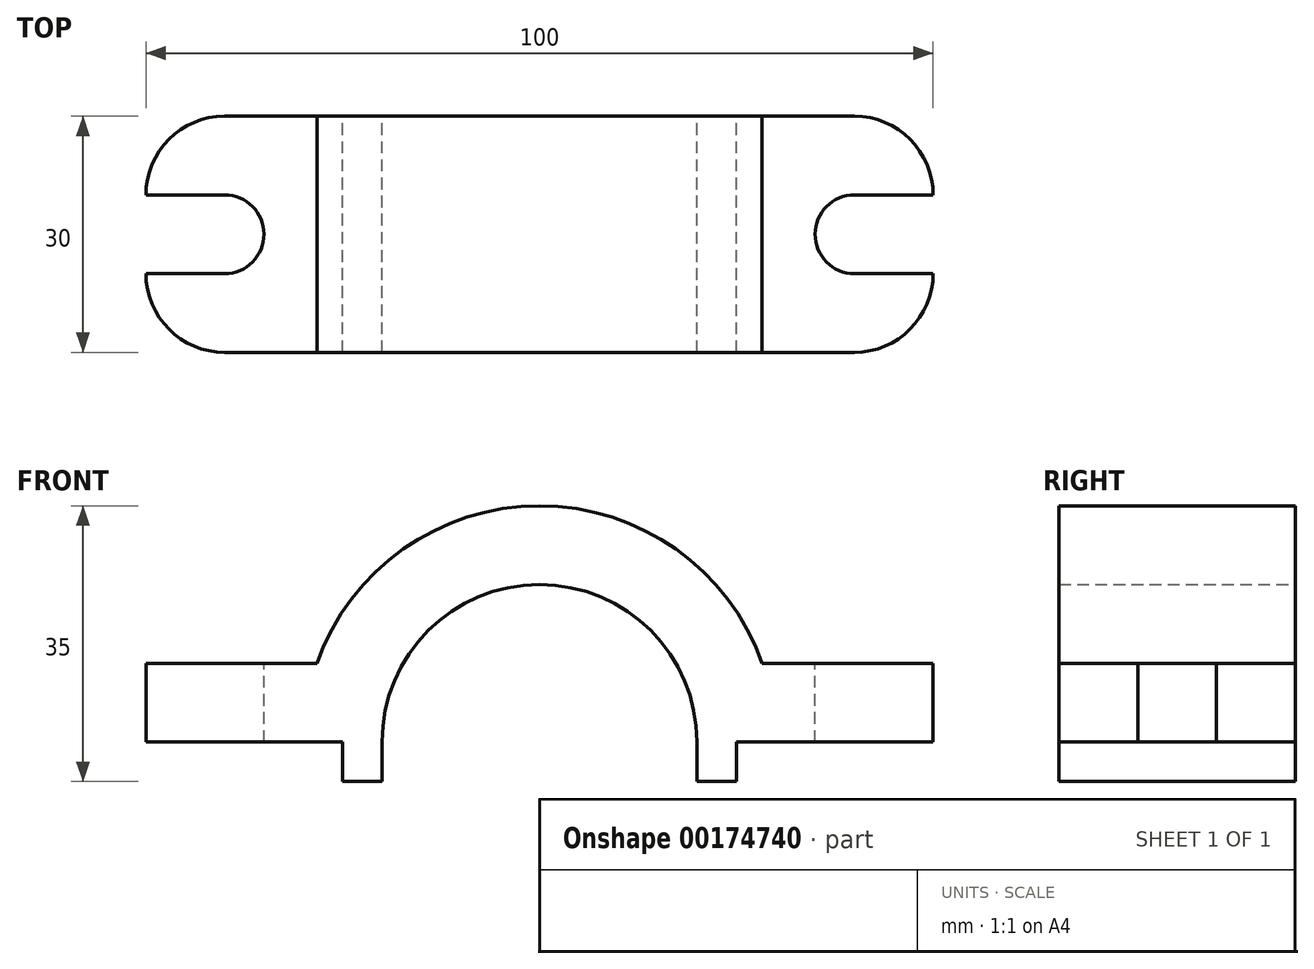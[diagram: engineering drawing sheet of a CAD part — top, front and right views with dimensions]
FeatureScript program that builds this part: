
annotation { "Feature Type Name" : "Feature", "Feature Type Description" : "" }
export const myFeature = defineFeature(function(context is Context, id is Id, definition is map)
    precondition{}
    {
        {
            var Q0;
            Q0=qCreatedBy(makeId("Front.planeOp"),FACE);
            var sketch = newSketch(context, id + "F0", { "sketchPlane" : qUnion([Q0])});
            skLineSegment(sketch, "E0.bottom", {"start": v(-50, 0) * mm, "end": v(-25, 0) * mm});
            skLineSegment(sketch, "E0.top", {"start": v(-50, 10) * mm, "end": v(-28.28, 10) * mm});
            skLineSegment(sketch, "E0.left", {"start": v(-50, 0) * mm, "end": v(-50, 10) * mm});
            skLineSegment(sketch, "E0.right", {"start": v(50, 0) * mm, "end": v(50, 10) * mm});
            skArc(sketch, "E1", {"start": v(28.28, 10) * mm, "mid": v(0, 30) * mm, "end": v(-28.28, 10) * mm});
            skLineSegment(sketch, "E2.trimOffspring", {"start": v(28.28, 10) * mm, "end": v(50, 10) * mm});
            skArc(sketch, "E3", {"start": v(20, 0) * mm, "mid": v(0, 20) * mm, "end": v(-20, 0) * mm});
            skLineSegment(sketch, "E4.trimOffspring", {"start": v(25, 0) * mm, "end": v(50, 0) * mm});
            skLineSegment(sketch, "E5.top", {"start": v(-20, -5) * mm, "end": v(-25, -5) * mm});
            skLineSegment(sketch, "E5.left", {"start": v(-20, 0) * mm, "end": v(-20, -5) * mm});
            skLineSegment(sketch, "E5.right", {"start": v(-25, 0) * mm, "end": v(-25, -5) * mm});
            skLineSegment(sketch, "E6.top", {"start": v(20, -5) * mm, "end": v(25, -5) * mm});
            skLineSegment(sketch, "E6.left", {"start": v(20, 0) * mm, "end": v(20, -5) * mm});
            skLineSegment(sketch, "E6.right", {"start": v(25, 0) * mm, "end": v(25, -5) * mm});
            skSolve(sketch);
        }
        {
            var Q0;
            Q0=makeQuery(id+"F0.imprint","IMPRINT",FACE,{"disambiguationData":[TD([[makeQuery(id+"F0.imprint","IMPRINT",EDGE,{"derivedFrom":sQuery(id+"F0.wireOp",EDGE,"E0.bottom")}),1.0]])]});
            extrude(context, id + "F1", {"entities" : qUnion([Q0]), "endBound" : BoundingType.SYMMETRIC, "depth" : 30 * mm});
        }
        {
            var Q0;
            Q0=makeQuery(id+"F1.opExtrude","CAP_EDGE",EDGE,{"disambiguationData":[OSD([sQuery(id+"F0.wireOp",EDGE,"E0.left")])],"isStart":false});
            var Q1;
            Q1=makeQuery(id+"F1.opExtrude","CAP_EDGE",EDGE,{"disambiguationData":[OSD([sQuery(id+"F0.wireOp",EDGE,"E0.right")])],"isStart":false});
            var Q2;
            Q2=makeQuery(id+"F1.opExtrude","CAP_EDGE",EDGE,{"disambiguationData":[OSD([sQuery(id+"F0.wireOp",EDGE,"E0.right")])],"isStart":true});
            var Q3;
            Q3=makeQuery(id+"F1.opExtrude","CAP_EDGE",EDGE,{"disambiguationData":[OSD([sQuery(id+"F0.wireOp",EDGE,"E0.left")])],"isStart":true});
            fillet(context, id + "F2", {"entities" : qUnion([Q0, Q1, Q2, Q3]), "radius" : 10 * mm, "tangentPropagation" : true, "allowEdgeOverflow" : false});
        }
        {
            var Q0;
            Q0=makeQuery(id+"F1.opExtrude","SWEPT_FACE",FACE,{"disambiguationData":[OSD([sQuery(id+"F0.wireOp",EDGE,"E0.top")])]});
            var sketch = newSketch(context, id + "F3", { "sketchPlane" : qUnion([Q0])});
            skLineSegment(sketch, "E7.bottom", {"start": v(-50, 5) * mm, "end": v(-40, 5) * mm});
            skLineSegment(sketch, "E7.top", {"start": v(-50, -5) * mm, "end": v(-40, -5) * mm});
            skLineSegment(sketch, "E7.left", {"start": v(-50, 5) * mm, "end": v(-50, -5) * mm});
            skArc(sketch, "E8", {"start": v(-40, -5) * mm, "mid": v(-35, 0) * mm, "end": v(-40, 5) * mm});
            skSolve(sketch);
        }
        {
            var Q0;
            Q0 = qSketchRegion(id + "F3", true);
            extrude(context, id + "F4", {"entities" : qUnion([Q0]), "operationType" : NewBodyOperationType.REMOVE, "endBound" : BoundingType.UP_TO_NEXT, "oppositeDirection" : true, "depth" : 25 * mm});
        }
        {
            var Q0;
            Q0=makeQuery(id+"F1.opExtrude","SWEPT_FACE",FACE,{"disambiguationData":[OSD([sQuery(id+"F0.wireOp",EDGE,"E2.trimOffspring")])]});
            var sketch = newSketch(context, id + "F5", { "sketchPlane" : qUnion([Q0])});
            skLineSegment(sketch, "E9.bottom", {"start": v(50, 5) * mm, "end": v(40, 5) * mm});
            skLineSegment(sketch, "E9.top", {"start": v(50, -5) * mm, "end": v(40, -5) * mm});
            skLineSegment(sketch, "E9.left", {"start": v(50, 5) * mm, "end": v(50, -5) * mm});
            skArc(sketch, "E10", {"start": v(40, 5) * mm, "mid": v(35, 0) * mm, "end": v(40, -5) * mm});
            skSolve(sketch);
        }
        {
            var Q0;
            Q0=makeQuery(id+"F5.imprint","IMPRINT",FACE,{"disambiguationData":[TD([[makeQuery(id+"F5.imprint","IMPRINT",EDGE,{"derivedFrom":sQuery(id+"F5.wireOp",EDGE,"E9.bottom")}),1.0]])]});
            extrude(context, id + "F6", {"entities" : qUnion([Q0]), "operationType" : NewBodyOperationType.REMOVE, "endBound" : BoundingType.UP_TO_NEXT, "oppositeDirection" : true, "depth" : 25 * mm});
        }
    });
